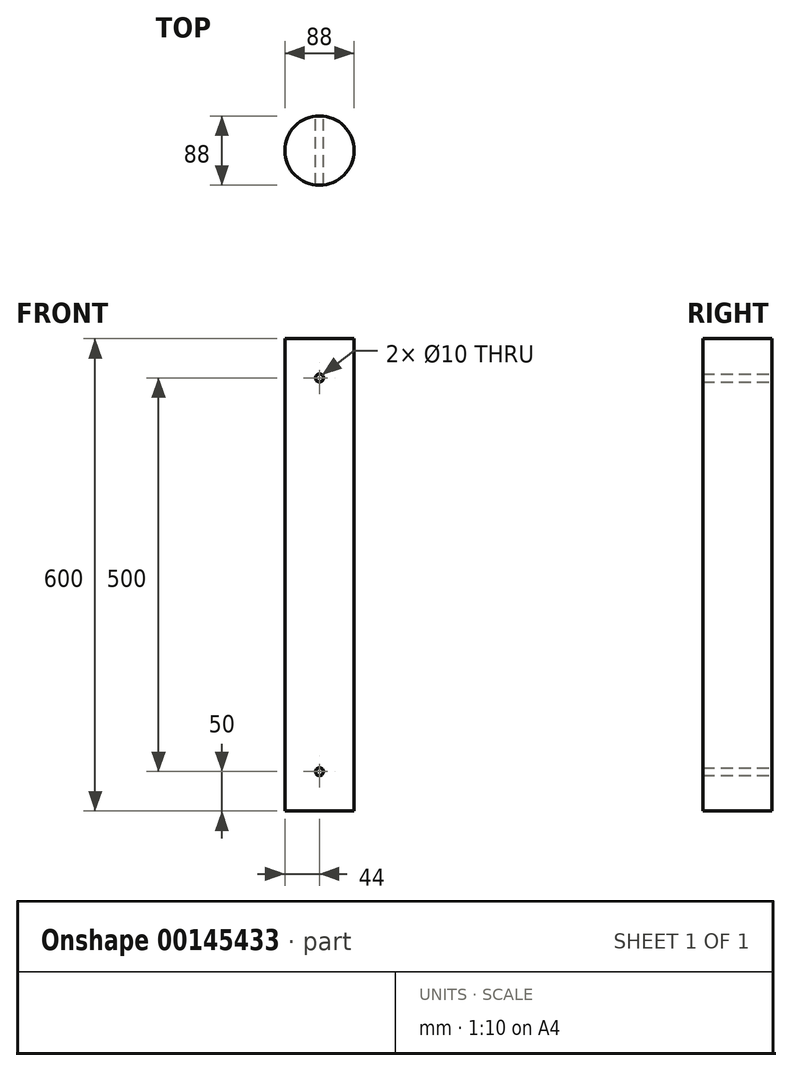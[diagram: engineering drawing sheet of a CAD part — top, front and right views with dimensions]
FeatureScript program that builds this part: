
annotation { "Feature Type Name" : "Feature", "Feature Type Description" : "" }
export const myFeature = defineFeature(function(context is Context, id is Id, definition is map)
    precondition{}
    {
        {
            var Q0;
            Q0=qCreatedBy(makeId("Top.planeOp"),FACE);
            var sketch = newSketch(context, id + "F0", { "sketchPlane" : qUnion([Q0])});
            skCircle(sketch, "E0", {"center": v(0, 0) * mm, "radius": 44 * mm});
            skSolve(sketch);
        }
        {
            var Q0;
            Q0=qSketchRegion(id+"F0",true);
            extrude(context, id + "F1", {"entities" : qUnion([Q0]), "depth" : 600 * mm, "symmetric" : true});
        }
        {
            var Q0;
            Q0=qCreatedBy(makeId("Front.planeOp"),FACE);
            var sketch = newSketch(context, id + "F2", { "sketchPlane" : qUnion([Q0])});
            skCircle(sketch, "E1", {"center": v(0, -250) * mm, "radius": 5 * mm});
            skCircle(sketch, "E2.MirrorC", {"center": v(0, 250) * mm, "radius": 5 * mm});
            skSolve(sketch);
        }
        {
            var Q0;
            Q0 = qSketchRegion(id + "F2", true);
            extrude(context, id + "F3", {"entities" : qUnion([Q0]), "operationType" : NewBodyOperationType.REMOVE, "depth" : 300 * mm, "symmetric" : true});
        }
    });
